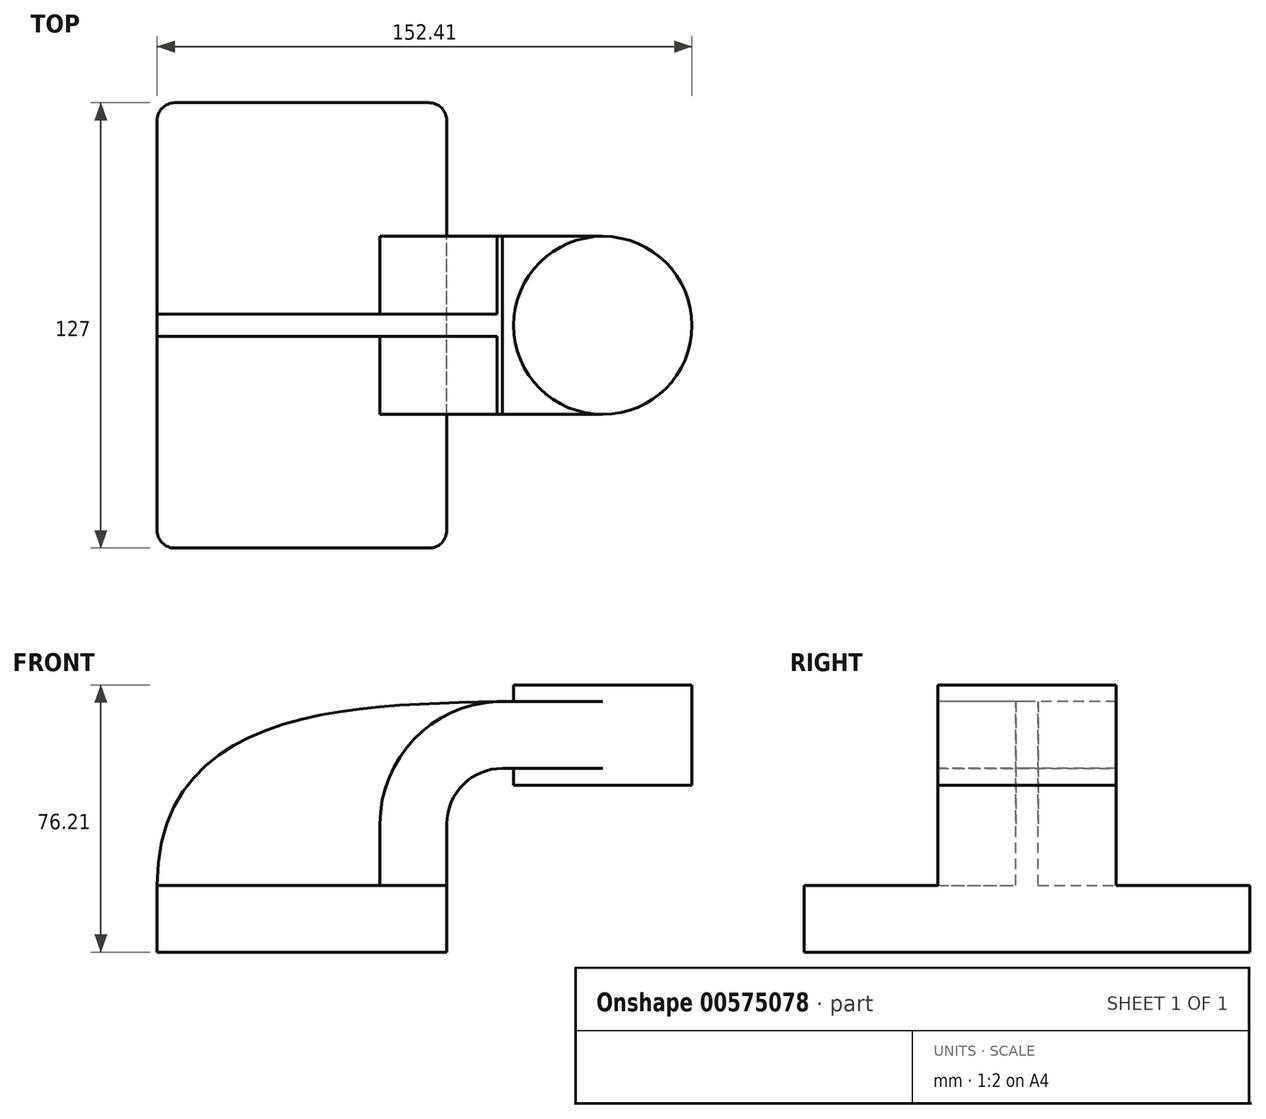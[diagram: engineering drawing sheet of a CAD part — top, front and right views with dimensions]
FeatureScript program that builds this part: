
annotation { "Feature Type Name" : "Feature", "Feature Type Description" : "" }
export const myFeature = defineFeature(function(context is Context, id is Id, definition is map)
    precondition{}
    {
        {
            var Q0;
            Q0=qCreatedBy(makeId("Front.planeOp"),FACE);
            var sketch = newSketch(context, id + "F0", { "sketchPlane" : qUnion([Q0])});
            skLineSegment(sketch, "E0.bottom", {"start": v(41.28, 9.52) * mm, "end": v(-41.28, 9.52) * mm});
            skLineSegment(sketch, "E0.top", {"start": v(41.28, -9.53) * mm, "end": v(-41.28, -9.53) * mm});
            skLineSegment(sketch, "E0.left", {"start": v(41.28, 9.52) * mm, "end": v(41.28, -9.53) * mm});
            skLineSegment(sketch, "E0.right", {"start": v(-41.28, 9.52) * mm, "end": v(-41.28, -9.53) * mm});
            skPoint(sketch, "E0.middle", {"position": v(0, 0) * mm});
            skLineSegment(sketch, "E1.bottom", {"start": v(60.32, 66.68) * mm, "end": v(111.12, 66.68) * mm});
            skLineSegment(sketch, "E1.top", {"start": v(60.32, 38.1) * mm, "end": v(111.12, 38.1) * mm});
            skLineSegment(sketch, "E1.left", {"start": v(60.32, 66.68) * mm, "end": v(60.32, 38.1) * mm});
            skLineSegment(sketch, "E1.right", {"start": v(111.12, 66.68) * mm, "end": v(111.12, 38.1) * mm});
            skLineSegment(sketch, "E2", {"start": v(41.28, 9.52) * mm, "end": v(41.28, 27) * mm});
            skArc(sketch, "E3", {"start": v(41.27, 27) * mm, "mid": v(45.92, 38.23) * mm, "end": v(57.15, 42.88) * mm});
            skLineSegment(sketch, "E4", {"start": v(57.15, 42.88) * mm, "end": v(85.72, 42.88) * mm});
            skPoint(sketch, "E4.endSnap0", {"position": v(85.72, 38.1) * mm});
            skLineSegment(sketch, "E5.0", {"start": v(57.15, 61.93) * mm, "end": v(85.72, 61.93) * mm});
            skArc(sketch, "E6.1", {"start": v(22.23, 27) * mm, "mid": v(32.45, 51.7) * mm, "end": v(57.15, 61.93) * mm});
            skLineSegment(sketch, "E6.2", {"start": v(22.22, 9.52) * mm, "end": v(22.22, 27) * mm});
            skLineSegment(sketch, "E7", {"start": v(85.72, 38.1) * mm, "end": v(85.72, 66.68) * mm});
            skFitSpline(sketch, "E8", {"points": [v(-41.28, 9.53) * mm, v(57.15, 61.93) * mm], "startDerivative": vector(0.5, 155.82) * mm, "endDerivative": vector(120.76, 2.8) * mm});
            skSolve(sketch);
        }
        {
            var Q0;
            Q0=makeQuery(id+"F0.imprint","IMPRINT",FACE,{"disambiguationData":[TD([[makeQuery(id+"F0.imprint","IMPRINT",EDGE,{"derivedFrom":sQuery(id+"F0.wireOp",EDGE,"E0.top")}),-1.0]])]});
            extrude(context, id + "F1", {"entities" : qUnion([Q0]), "depth" : 127 * mm, "offsetDistance" : 25.4 * mm, "symmetric" : true});
        }
        {
            var Q0;
            {var subQ1=sQuery(id+"F0.wireOp",EDGE,"E2");Q0=makeQuery(id+"F0.imprint","IMPRINT",FACE,{"disambiguationData":[TD([[makeQuery(id+"F0.imprint","IMPRINT",EDGE,{"derivedFrom":subQ1}),1.0]])]});}
            var Q1;
            {var subQ0=sQuery(id+"F0.wireOp",EDGE,"E5.0");var subQ1=sQuery(id+"F0.wireOp",EDGE,"E1.left");var subQ2=makeQuery(id+"F0.imprint","INTERSECT",VERTEX,{"derivedFrom":[subQ1,subQ0]});Q1=makeQuery(id+"F0.imprint","IMPRINT",FACE,{"disambiguationData":[TD([[makeQuery(id+"F0.imprint","IMPRINT",EDGE,{"disambiguationData":[TD([[subQ2,-1.0]])],"derivedFrom":subQ1}),1.0]])]});}
            extrude(context, id + "F2", {"entities" : qUnion([Q0, Q1]), "operationType" : NewBodyOperationType.ADD, "depth" : 50.8 * mm, "offsetDistance" : 25.4 * mm, "symmetric" : true});
        }
        {
            var Q0;
            {var subQ3=sQuery(id+"F0.wireOp",EDGE,"E6.2");Q0=makeQuery(id+"F0.imprint","IMPRINT",FACE,{"disambiguationData":[TD([[makeQuery(id+"F0.imprint","IMPRINT",EDGE,{"derivedFrom":subQ3}),1.0]])]});}
            extrude(context, id + "F3", {"entities" : qUnion([Q0]), "operationType" : NewBodyOperationType.ADD, "depth" : 6.35 * mm, "offsetDistance" : 25.4 * mm, "symmetric" : true});
        }
        {
            var Q0;
            {var subQ4=sQuery(id+"F0.wireOp",EDGE,"E1.right");Q0=makeQuery(id+"F0.imprint","IMPRINT",FACE,{"disambiguationData":[TD([[makeQuery(id+"F0.imprint","IMPRINT",EDGE,{"derivedFrom":subQ4}),-1.0]])]});}
            var Q1;
            Q1=sQuery(id+"F0.wireOp",EDGE,"E7");
            revolve(context, id + "F4", {"operationType" : NewBodyOperationType.ADD, "entities" : qUnion([Q0]), "axis" : qUnion([Q1]), "revolveType" : RevolveType.FULL});
        }
        {
            var Q0;
            Q0=makeQuery(id+"F1.opExtrude","CAP_EDGE",EDGE,{"disambiguationData":[OSD([sQuery(id+"F0.wireOp",EDGE,"E0.right")])],"isStart":false});
            var Q1;
            Q1=makeQuery(id+"F1.opExtrude","CAP_EDGE",EDGE,{"disambiguationData":[OSD([sQuery(id+"F0.wireOp",EDGE,"E0.left")])],"isStart":false});
            var Q2;
            Q2=makeQuery(id+"F1.opExtrude","CAP_EDGE",EDGE,{"disambiguationData":[OSD([sQuery(id+"F0.wireOp",EDGE,"E0.left")])],"isStart":true});
            var Q3;
            Q3=makeQuery(id+"F1.opExtrude","CAP_EDGE",EDGE,{"disambiguationData":[OSD([sQuery(id+"F0.wireOp",EDGE,"E0.right")])],"isStart":true});
            fillet(context, id + "F5", {"entities" : qUnion([Q0, Q1, Q2, Q3]), "radius" : 5.08 * mm, "tangentPropagation" : true, "allowEdgeOverflow" : false});
        }
    });
